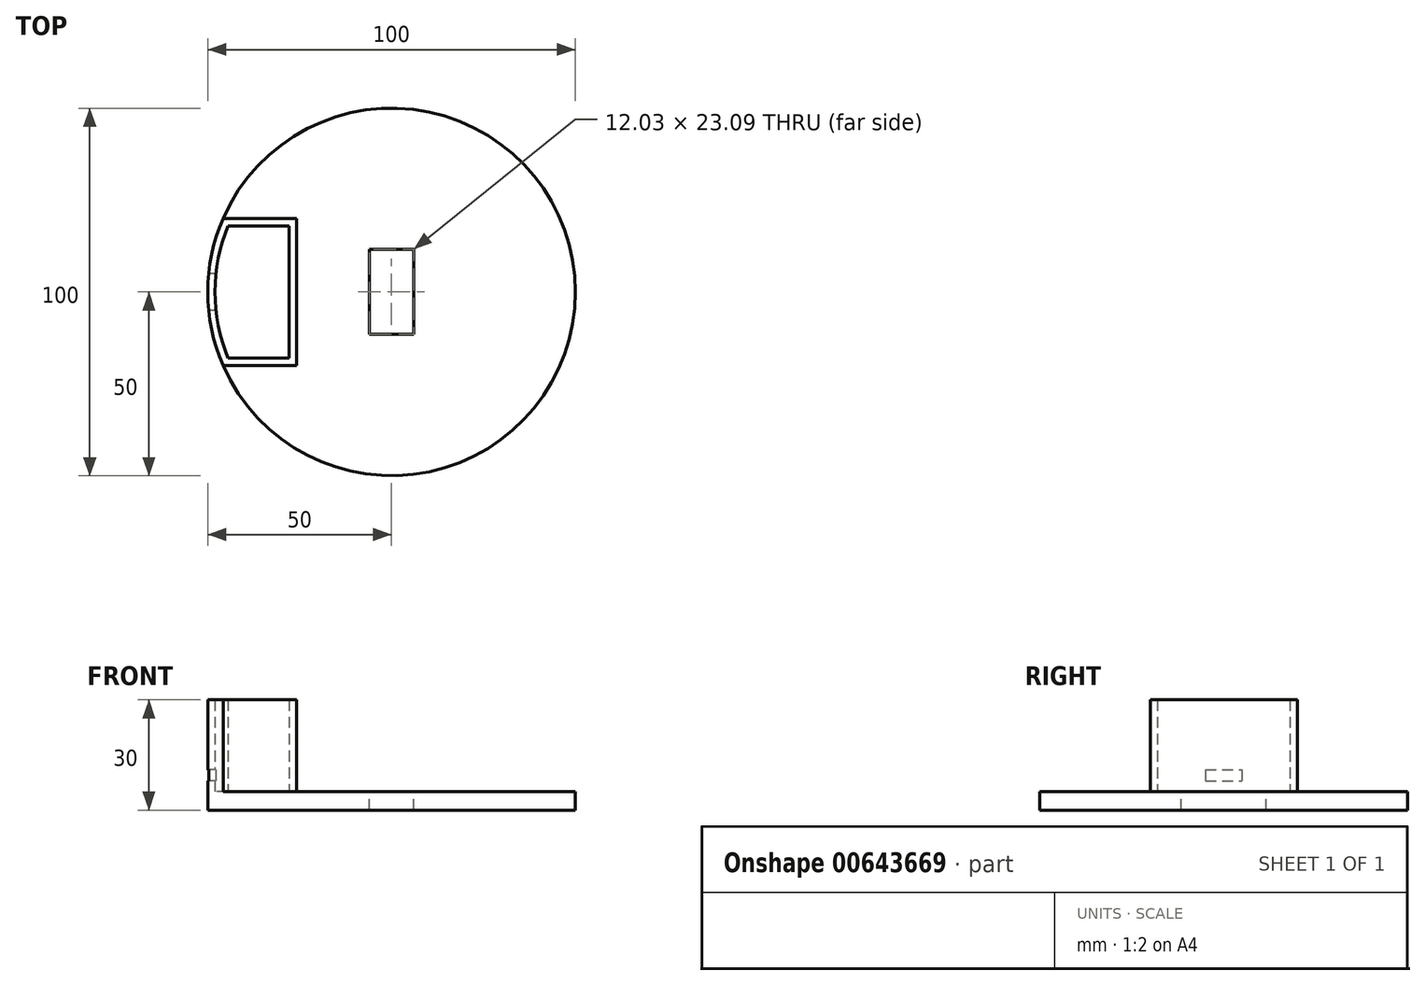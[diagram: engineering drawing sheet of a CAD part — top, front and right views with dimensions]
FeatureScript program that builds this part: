
annotation { "Feature Type Name" : "Feature", "Feature Type Description" : "" }
export const myFeature = defineFeature(function(context is Context, id is Id, definition is map)
    precondition{}
    {
        {
            var Q0;
            Q0=qCreatedBy(makeId("Top.planeOp"),FACE);
            var sketch = newSketch(context, id + "F0", { "sketchPlane" : qUnion([Q0])});
            skCircle(sketch, "E0", {"center": v(0, 0) * mm, "radius": 50 * mm});
            skSolve(sketch);
        }
        {
            var Q0;
            Q0=makeQuery(id+"F0.imprint","IMPRINT",FACE,{"disambiguationData":[TD([[makeQuery(id+"F0.imprint","IMPRINT",EDGE,{"derivedFrom":sQuery(id+"F0.wireOp",EDGE,"E0")}),1.0]])]});
            extrude(context, id + "F1", {"entities" : qUnion([Q0]), "depth" : 5 * mm, "offsetDistance" : 25 * mm});
        }
        {
            var Q0;
            Q0=makeQuery(id+"F1.opExtrude","CAP_FACE",FACE,{"disambiguationData":[OSD([sQuery(id+"F0.wireOp",EDGE,"E0")])],"isStart":false});
            var sketch = newSketch(context, id + "F2", { "sketchPlane" : qUnion([Q0])});
            skArc(sketch, "E1", {"start": v(-45.83, 20) * mm, "mid": v(-50, 0) * mm, "end": v(-45.83, -20) * mm});
            skLineSegment(sketch, "E2.bottom", {"start": v(-45.83, 20) * mm, "end": v(-25.83, 20) * mm});
            skLineSegment(sketch, "E2.top", {"start": v(-45.83, -20) * mm, "end": v(-25.83, -20) * mm});
            skLineSegment(sketch, "E2.right", {"start": v(-25.83, 20) * mm, "end": v(-25.83, -20) * mm});
            skSolve(sketch);
        }
        {
            var Q0;
            Q0=makeQuery(id+"F2.imprint","IMPRINT",FACE,{"disambiguationData":[TD([[makeQuery(id+"F2.imprint","IMPRINT",EDGE,{"derivedFrom":sQuery(id+"F2.wireOp",EDGE,"E1")}),1.0]])]});
            extrude(context, id + "F3", {"entities" : qUnion([Q0]), "operationType" : NewBodyOperationType.ADD, "depth" : 25 * mm, "offsetDistance" : 25 * mm});
        }
        {
            var Q0;
            Q0=makeQuery(id+"F3.opExtrude","CAP_FACE",FACE,{"disambiguationData":[OSD([sQuery(id+"F2.wireOp",EDGE,"E1"),sQuery(id+"F2.wireOp",EDGE,"E2.bottom"),sQuery(id+"F2.wireOp",EDGE,"E2.top"),sQuery(id+"F2.wireOp",EDGE,"E2.right")])],"isStart":false});
            shell(context, id + "F4", {"entities" : qUnion([Q0]), "thickness" : 2 * mm});
        }
        {
            var Q0;
            Q0=qCreatedBy(makeId("Right.planeOp"),FACE);
            cPlane(context, id + "F5", {"entities" : qUnion([Q0]), "cplaneType" : CPlaneType.OFFSET, "offset" : 50 * mm, "oppositeDirection" : true, "width" : 150 * mm, "height" : 150 * mm});
        }
        {
            var Q0;
            Q0=qCreatedBy(id+"F5.planeOp",FACE);
            var sketch = newSketch(context, id + "F6", { "sketchPlane" : qUnion([Q0])});
            skLineSegment(sketch, "E3.bottom", {"start": v(5, 11) * mm, "end": v(-5, 11) * mm});
            skLineSegment(sketch, "E3.top", {"start": v(5, 8) * mm, "end": v(-5, 8) * mm});
            skLineSegment(sketch, "E3.left", {"start": v(5, 11) * mm, "end": v(5, 8) * mm});
            skLineSegment(sketch, "E3.right", {"start": v(-5, 11) * mm, "end": v(-5, 8) * mm});
            skPoint(sketch, "E3.middle", {"position": v(0, 9.5) * mm});
            skSolve(sketch);
        }
        {
            var Q0;
            Q0=makeQuery(id+"F6.imprint","IMPRINT",FACE,{"disambiguationData":[TD([[makeQuery(id+"F6.imprint","IMPRINT",EDGE,{"derivedFrom":sQuery(id+"F6.wireOp",EDGE,"E3.bottom")}),1.0]])]});
            extrude(context, id + "F7", {"entities" : qUnion([Q0]), "operationType" : NewBodyOperationType.REMOVE, "depth" : 3 * mm, "offsetDistance" : 25 * mm});
        }
        {
            var Q0;
            Q0=makeQuery(id+"F1.opExtrude","CAP_FACE",FACE,{"disambiguationData":[OSD([sQuery(id+"F0.wireOp",EDGE,"E0")])],"isStart":false});
            var sketch = newSketch(context, id + "F8", { "sketchPlane" : qUnion([Q0])});
            skLineSegment(sketch, "E4.bottom", {"start": v(-6.02, 11.54) * mm, "end": v(6.02, 11.54) * mm});
            skLineSegment(sketch, "E4.top", {"start": v(-6.02, -11.54) * mm, "end": v(6.02, -11.54) * mm});
            skLineSegment(sketch, "E4.left", {"start": v(-6.02, 11.54) * mm, "end": v(-6.02, -11.54) * mm});
            skLineSegment(sketch, "E4.right", {"start": v(6.02, 11.54) * mm, "end": v(6.02, -11.54) * mm});
            skPoint(sketch, "E4.middle", {"position": v(0, 0) * mm});
            skSolve(sketch);
        }
        {
            var Q0;
            Q0=makeQuery(id+"F8.imprint","IMPRINT",FACE,{"disambiguationData":[TD([[makeQuery(id+"F8.imprint","IMPRINT",EDGE,{"derivedFrom":sQuery(id+"F8.wireOp",EDGE,"E4.bottom")}),-1.0]])]});
            extrude(context, id + "F9", {"entities" : qUnion([Q0]), "operationType" : NewBodyOperationType.REMOVE, "oppositeDirection" : true, "depth" : 25 * mm, "offsetDistance" : 25 * mm});
        }
        {
            var Q0;
            Q0=makeQuery(id+"F1.opExtrude","CAP_FACE",FACE,{"disambiguationData":[OSD([sQuery(id+"F0.wireOp",EDGE,"E0")])],"isStart":true});
            var sketch = newSketch(context, id + "F10", { "sketchPlane" : qUnion([Q0])});
            skCircle(sketch, "E5", {"center": v(0, 0) * mm, "radius": 50 * mm});
            skSolve(sketch);
        }
        {
            var Q0;
            Q0=makeQuery(id+"F10.imprint","IMPRINT",FACE,{"disambiguationData":[TD([[makeQuery(id+"F10.imprint","IMPRINT",EDGE,{"derivedFrom":sQuery(id+"F10.wireOp",EDGE,"E5")}),-1.0]])]});
            extrude(context, id + "F11", {"entities" : qUnion([Q0]), "operationType" : NewBodyOperationType.ADD, "oppositeDirection" : true, "depth" : 5 * mm, "offsetDistance" : 25 * mm});
        }
    });
